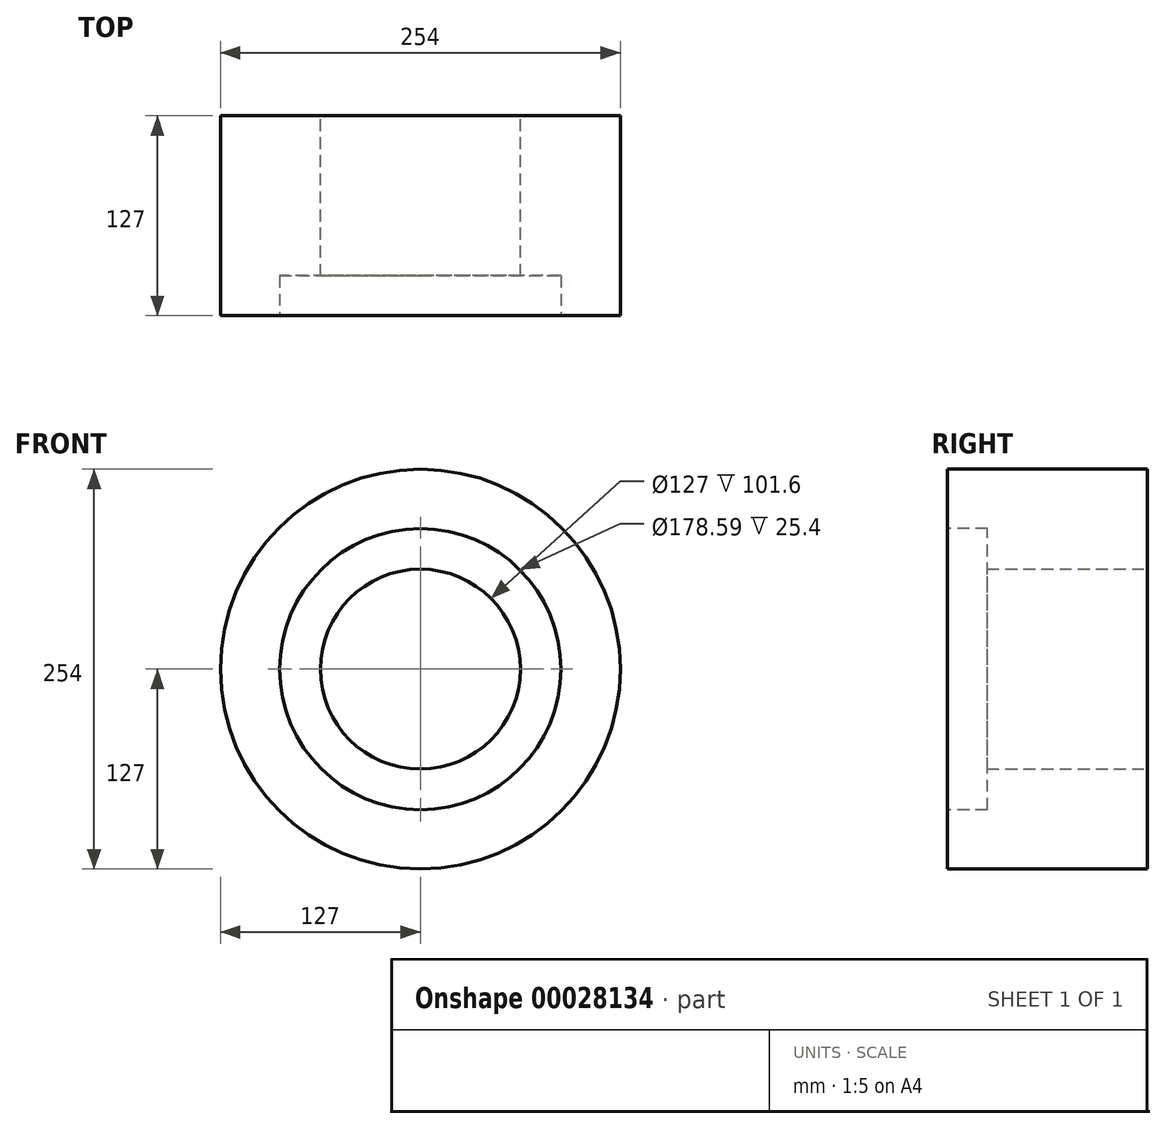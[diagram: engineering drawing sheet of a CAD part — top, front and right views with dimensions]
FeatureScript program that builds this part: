
annotation { "Feature Type Name" : "Feature", "Feature Type Description" : "" }
export const myFeature = defineFeature(function(context is Context, id is Id, definition is map)
    precondition{}
    {
        {
            var Q0;
            Q0=qCreatedBy(makeId("Front.planeOp"),FACE);
            var sketch = newSketch(context, id + "F0", { "sketchPlane" : qUnion([Q0])});
            skCircle(sketch, "E0", {"center": v(0, 0) * mm, "radius": 127 * mm});
            skCircle(sketch, "E1", {"center": v(0, 0) * mm, "radius": 63.5 * mm});
            skSolve(sketch);
        }
        {
            var Q0;
            Q0=makeQuery(id+"F0.imprint","IMPRINT",FACE,{"disambiguationData":[TD([[makeQuery(id+"F0.imprint","IMPRINT",EDGE,{"derivedFrom":sQuery(id+"F0.wireOp",EDGE,"E0")}),1.0]])]});
            extrude(context, id + "F1", {"entities" : qUnion([Q0]), "depth" : 127 * mm});
        }
        {
            var Q0;
            Q0=makeQuery(id+"F1.opExtrude","CAP_FACE",FACE,{"disambiguationData":[OSD([sQuery(id+"F0.wireOp",EDGE,"E0"),sQuery(id+"F0.wireOp",EDGE,"E1")])],"isStart":false});
            var sketch = newSketch(context, id + "F2", { "sketchPlane" : qUnion([Q0])});
            skCircle(sketch, "E2", {"center": v(0, 0) * mm, "radius": 89.3 * mm});
            skSolve(sketch);
        }
        {
            var Q0;
            Q0=makeQuery(id+"F2.imprint","IMPRINT",FACE,{"disambiguationData":[TD([[makeQuery(id+"F2.imprint","IMPRINT",EDGE,{"derivedFrom":sQuery(id+"F2.wireOp",EDGE,"E2")}),1.0]])]});
            extrude(context, id + "F3", {"entities" : qUnion([Q0]), "operationType" : NewBodyOperationType.REMOVE, "oppositeDirection" : true, "depth" : 25.4 * mm});
        }
    });
